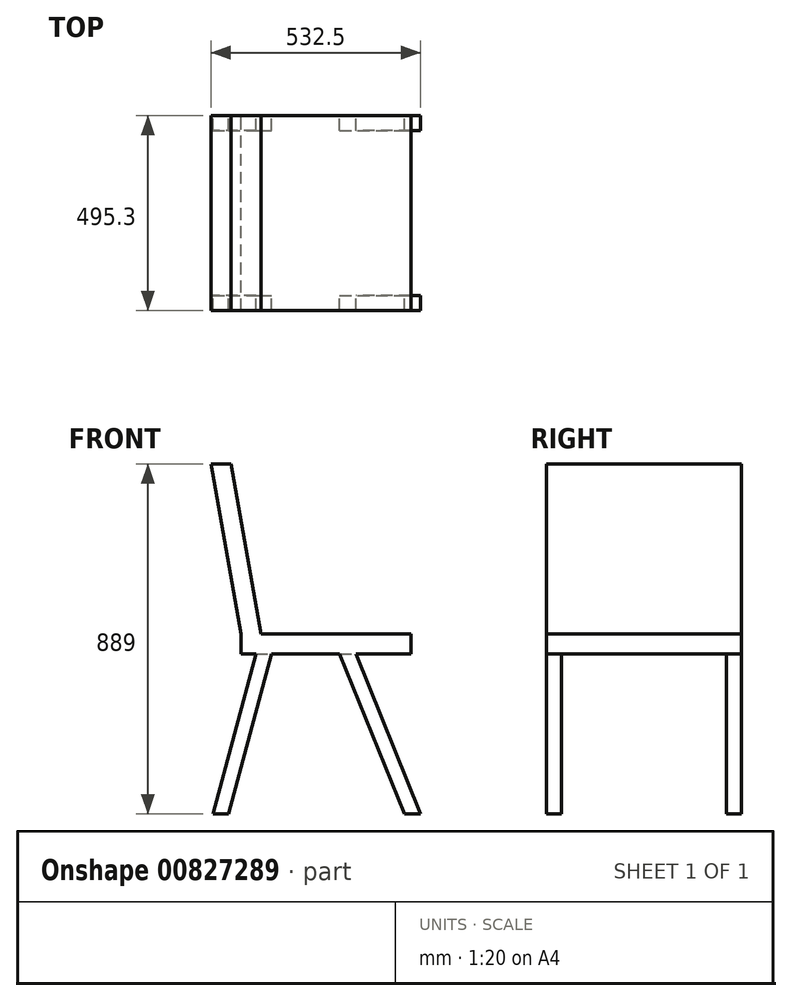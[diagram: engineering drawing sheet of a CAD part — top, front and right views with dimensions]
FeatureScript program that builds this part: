
annotation { "Feature Type Name" : "Feature", "Feature Type Description" : "" }
export const myFeature = defineFeature(function(context is Context, id is Id, definition is map)
    precondition{}
    {
        {
            var Q0;
            Q0=qCreatedBy(makeId("Front.planeOp"),FACE);
            var sketch = newSketch(context, id + "F0", { "sketchPlane" : qUnion([Q0])});
            skLineSegment(sketch, "E0", {"start": v(-480.91, 889) * mm, "end": v(-404.71, 457.2) * mm});
            skLineSegment(sketch, "E1", {"start": v(-404.71, 457.2) * mm, "end": v(-24.5, 457.2) * mm});
            skLineSegment(sketch, "E2", {"start": v(-24.5, 457.2) * mm, "end": v(-24.5, 406.4) * mm});
            skLineSegment(sketch, "E3", {"start": v(-24.5, 406.4) * mm, "end": v(-456.3, 406.4) * mm});
            skLineSegment(sketch, "E4", {"start": v(-456.3, 406.4) * mm, "end": v(-456.3, 457.2) * mm});
            skLineSegment(sketch, "E5", {"start": v(-456.3, 457.2) * mm, "end": v(-532.5, 889) * mm});
            skLineSegment(sketch, "E6", {"start": v(-532.5, 889) * mm, "end": v(-480.91, 889) * mm});
            skLineSegment(sketch, "E7", {"start": v(-418.2, 406.4) * mm, "end": v(-527.1, 0) * mm});
            skLineSegment(sketch, "E8", {"start": v(-527.1, 0) * mm, "end": v(-487.65, 0) * mm});
            skLineSegment(sketch, "E9", {"start": v(-487.65, 0) * mm, "end": v(-378.75, 406.4) * mm});
            skLineSegment(sketch, "E10", {"start": v(-205.29, 406.4) * mm, "end": v(-41.1, 0) * mm});
            skLineSegment(sketch, "E11", {"start": v(-41.1, 0) * mm, "end": v(0, 0) * mm});
            skLineSegment(sketch, "E12", {"start": v(0, 0) * mm, "end": v(-164.2, 406.4) * mm});
            skSolve(sketch);
        }
        {
            var Q0;
            Q0=qSketchRegion(id+"F0",true);
            extrude(context, id + "F1", {"entities" : qUnion([Q0]), "depth" : 495.3 * mm});
        }
        {
            var Q0;
            Q0=qCreatedBy(makeId("Right.planeOp"),FACE);
            var sketch = newSketch(context, id + "F2", { "sketchPlane" : qUnion([Q0])});
            skLineSegment(sketch, "E13.bottom", {"start": v(-457.2, 406.4) * mm, "end": v(-38.1, 406.4) * mm});
            skLineSegment(sketch, "E13.top", {"start": v(-457.2, 0) * mm, "end": v(-38.1, 0) * mm});
            skLineSegment(sketch, "E13.left", {"start": v(-457.2, 406.4) * mm, "end": v(-457.2, 0) * mm});
            skLineSegment(sketch, "E13.right", {"start": v(-38.1, 406.4) * mm, "end": v(-38.1, 0) * mm});
            skSolve(sketch);
        }
        {
            var Q0;
            Q0=qSketchRegion(id+"F2",true);
            extrude(context, id + "F3", {"entities" : qUnion([Q0]), "operationType" : NewBodyOperationType.REMOVE, "endBound" : BoundingType.THROUGH_ALL, "oppositeDirection" : true, "depth" : 25.4 * mm});
        }
    });
